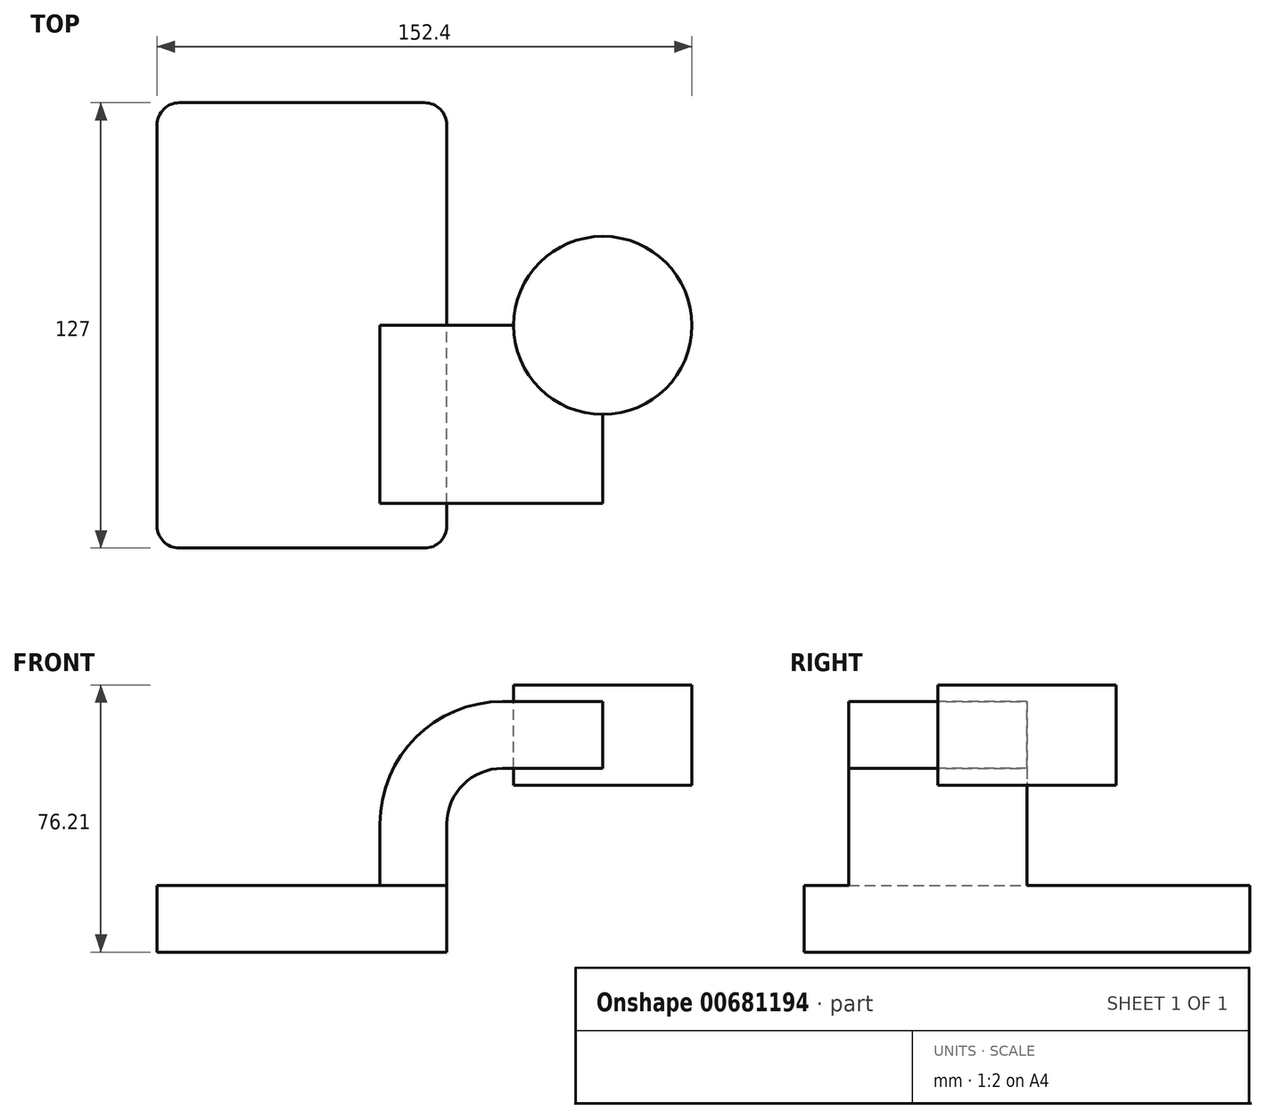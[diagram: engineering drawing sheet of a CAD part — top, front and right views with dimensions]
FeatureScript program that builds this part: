
annotation { "Feature Type Name" : "Feature", "Feature Type Description" : "" }
export const myFeature = defineFeature(function(context is Context, id is Id, definition is map)
    precondition{}
    {
        {
            var Q0;
            Q0=qCreatedBy(makeId("Front.planeOp"),FACE);
            var sketch = newSketch(context, id + "F0", { "sketchPlane" : qUnion([Q0])});
            skLineSegment(sketch, "E0.bottom", {"start": v(41.28, -9.52) * mm, "end": v(-41.28, -9.53) * mm});
            skLineSegment(sketch, "E0.top", {"start": v(41.28, 9.53) * mm, "end": v(-41.28, 9.52) * mm});
            skLineSegment(sketch, "E0.left", {"start": v(41.28, -9.52) * mm, "end": v(41.28, 9.53) * mm});
            skLineSegment(sketch, "E0.right", {"start": v(-41.28, -9.53) * mm, "end": v(-41.28, 9.52) * mm});
            skPoint(sketch, "E0.middle", {"position": v(0, 0) * mm});
            skLineSegment(sketch, "E1", {"start": v(41.28, 9.53) * mm, "end": v(41.28, 27) * mm});
            skArc(sketch, "E2", {"start": v(41.28, 27) * mm, "mid": v(45.92, 38.23) * mm, "end": v(57.15, 42.88) * mm});
            skLineSegment(sketch, "E3", {"start": v(57.15, 42.88) * mm, "end": v(85.73, 42.88) * mm});
            skLineSegment(sketch, "E4.bottom", {"start": v(111.13, 66.68) * mm, "end": v(60.33, 66.68) * mm});
            skLineSegment(sketch, "E4.top", {"start": v(111.13, 38.1) * mm, "end": v(60.33, 38.1) * mm});
            skLineSegment(sketch, "E4.left", {"start": v(111.13, 66.67) * mm, "end": v(111.13, 38.1) * mm});
            skLineSegment(sketch, "E4.right", {"start": v(60.33, 66.68) * mm, "end": v(60.33, 38.1) * mm});
            skPoint(sketch, "E4.middle", {"position": v(85.73, 52.39) * mm});
            skLineSegment(sketch, "E5.0", {"start": v(57.15, 61.93) * mm, "end": v(85.73, 61.93) * mm});
            skArc(sketch, "E5.1", {"start": v(22.23, 27) * mm, "mid": v(32.45, 51.7) * mm, "end": v(57.15, 61.93) * mm});
            skLineSegment(sketch, "E5.2", {"start": v(22.23, 9.53) * mm, "end": v(22.23, 27) * mm});
            skLineSegment(sketch, "E6", {"start": v(85.73, 42.88) * mm, "end": v(85.73, 66.68) * mm});
            skFitSpline(sketch, "E7", {"points": [v(-41.28, 9.52) * mm, v(57.15, 61.93) * mm], "startDerivative": vector(31.25, 25.65) * mm, "endDerivative": vector(171.45, -7.54) * mm});
            skLineSegment(sketch, "E8", {"start": v(85.73, 42.88) * mm, "end": v(85.73, 38.1) * mm});
            skLineSegment(sketch, "E9", {"start": v(85.73, 38.1) * mm, "end": v(85.73, 42.88) * mm});
            skLineSegment(sketch, "E10", {"start": v(85.73, 66.68) * mm, "end": v(85.73, 38.1) * mm});
            skSolve(sketch);
        }
        {
            var Q0;
            Q0=makeQuery(id+"F0.imprint","IMPRINT",FACE,{"disambiguationData":[TD([[makeQuery(id+"F0.imprint","IMPRINT",EDGE,{"derivedFrom":sQuery(id+"F0.wireOp",EDGE,"E0.bottom")}),-1.0]])]});
            extrude(context, id + "F1", {"entities" : qUnion([Q0]), "endBound" : BoundingType.SYMMETRIC, "depth" : 127 * mm, "offsetDistance" : 25.4 * mm});
        }
        {
            var Q0;
            {var subQ5=sQuery(id+"F0.wireOp",EDGE,"E1");Q0=makeQuery(id+"F0.imprint","IMPRINT",FACE,{"disambiguationData":[TD([[makeQuery(id+"F0.imprint","IMPRINT",EDGE,{"derivedFrom":subQ5}),1.0]])]});}
            var Q1;
            {var subQ0=sQuery(id+"F0.wireOp",EDGE,"E6");var subQ1=sQuery(id+"F0.wireOp",EDGE,"E3");var subQ2=makeQuery(id+"F0.imprint","INTERSECT",VERTEX,{"derivedFrom":[subQ1,subQ0]});Q1=makeQuery(id+"F0.imprint","IMPRINT",FACE,{"disambiguationData":[TD([[makeQuery(id+"F0.imprint","IMPRINT",EDGE,{"disambiguationData":[TD([[subQ2,1.0]])],"derivedFrom":subQ1}),1.0]])]});}
            extrude(context, id + "F2", {"entities" : qUnion([Q0, Q1]), "operationType" : NewBodyOperationType.ADD, "depth" : 50.8 * mm, "offsetDistance" : 25.4 * mm});
        }
        {
            var Q0;
            Q0=makeQuery(id+"F0.imprint","IMPRINT",FACE,{"disambiguationData":[TD([[makeQuery(id+"F0.imprint","IMPRINT",EDGE,{"derivedFrom":sQuery(id+"F0.wireOp",EDGE,"E5.1")}),1.0]])]});
            extrude(context, id + "F3", {"entities" : qUnion([Q0]), "operationType" : NewBodyOperationType.ADD, "depth" : 15.88 * mm, "offsetDistance" : 25.4 * mm});
        }
        {
            var Q0;
            {var subQ4=sQuery(id+"F0.wireOp",EDGE,"E4.left");Q0=makeQuery(id+"F0.imprint","IMPRINT",FACE,{"disambiguationData":[TD([[makeQuery(id+"F0.imprint","IMPRINT",EDGE,{"derivedFrom":subQ4}),-1.0]])]});}
            var Q1;
            Q1=sQuery(id+"F0.wireOp",EDGE,"E10");
            revolve(context, id + "F4", {"operationType" : NewBodyOperationType.ADD, "entities" : qUnion([Q0]), "axis" : qUnion([Q1]), "revolveType" : RevolveType.FULL});
        }
        {
            var Q0;
            Q0=makeQuery(id+"F1.opExtrude","CAP_EDGE",EDGE,{"disambiguationData":[OSD([sQuery(id+"F0.wireOp",EDGE,"E0.right")])],"isStart":false});
            var Q1;
            Q1=makeQuery(id+"F1.opExtrude","CAP_EDGE",EDGE,{"disambiguationData":[OSD([sQuery(id+"F0.wireOp",EDGE,"E0.left")])],"isStart":false});
            var Q2;
            Q2=makeQuery(id+"F1.opExtrude","CAP_EDGE",EDGE,{"disambiguationData":[OSD([sQuery(id+"F0.wireOp",EDGE,"E0.right")])],"isStart":true});
            var Q3;
            Q3=makeQuery(id+"F1.opExtrude","CAP_EDGE",EDGE,{"disambiguationData":[OSD([sQuery(id+"F0.wireOp",EDGE,"E0.left")])],"isStart":true});
            fillet(context, id + "F5", {"entities" : qUnion([Q0, Q1, Q2, Q3]), "radius" : 6.35 * mm, "tangentPropagation" : true, "allowEdgeOverflow" : false});
        }
    });
